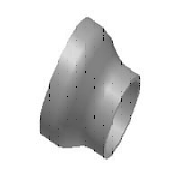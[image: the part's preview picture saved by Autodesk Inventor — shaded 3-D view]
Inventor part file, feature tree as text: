
AUTODESK INVENTOR PART (.ipt)
format: ipt  version: 2023.2 (Build 272271030, 271C)  size: 186,368 bytes
history: native  units: mm
features: other x4, revolve x1, sketch x1
ambient origin geometry x8: Origin, YZ Plane, XZ Plane, XY Plane, X Axis, Y Axis, Z Axis, Center Point
bodies: Solid1 (feature_tree)
feature tree (6):
  revolve  "Revolution1"  [1 undecoded]
  other  "Work Point1"
  other  "Work Point2"
  other  "Work Axis1"
  other  "Work Axis2"
  sketch  "Sketch1"  dims[d0=4.0mm d1=108.0mm d2=4.5mm d3=159.0mm d5=43.333333mm d6=43.333333mm d8=43.333333mm d10=90.0deg d13=130.0mm d15=43.333333mm]
note: 1 required parameter value undecoded (feature->parameter linkage not recoverable at this tier; creation-order binding heuristic only, values carry confidence <= 0.55)
